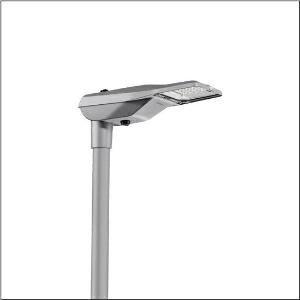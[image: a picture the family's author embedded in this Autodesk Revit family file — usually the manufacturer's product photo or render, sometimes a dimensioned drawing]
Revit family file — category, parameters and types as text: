
# Revit family: streetlight_sl_21_micro___st1_0a_5xe1d33t08db_ddb2
name_source: partatom
category: Lighting Fixtures
units: mm (PartAtom-declared; Revit-internal decimal feet)

## family parameters
Cut with Voids When Loaded = No
Host = Face
Light Source = No
Part Type = Normal
Room Calculation Point = No
Round Connector Dimension = Use Diameter
Shared = No

## types (1)
- --- (1 x LED, 5110 lm, 39.1 W, 3000K)
    Apparent Load = 39 VA
    CIE Flux Codes = 37 72 97 100 100
    Color Rendering = 70
    Color Temperature = 3000K
    Default Elevation = 1800 mm
    Description = Streetlight SL 21 micro, mast luminaire, primary light control with lens, of PMMA, primary optical cover: cover, of toughened safety glass, transparent, light distribution: ST1.0a, light emission: direct distribution, primary light characteristic: asymmetric, installation type: side-entry, post-top, LED, High Power LED, rated luminous flux: 5.110lm, luminous efficacy: 131lm/W, light colour: 730, colour temperature: 3000K, control: flexible luminous flux parameterisation, time-dependent luminous flux control, constant luminous flux control, overheat protection, presetting dimming logarithmic, mains connection: 220..240V, AC, 50/60Hz, start of lifetime: 39W, end of service life: 41W, reduction: 18W, luminaire housing, of diecast aluminium, powder-coated, Siteco® metallic grey (DB 702S), corrosivity category C5 mid according to DIN EN ISO 12944, please order mast flange separately, inclination adjustable: 0°, 5°, 10°, 15°, sealing non-destructively replaceable, multi-level sealing system, length: 528mm, width: 235mm, height: 110mm, mast flange for spigot size: 42mm (side-entry): 5XC10008XM4, 60/48mm (side-entry/post-top): 5XC10108XM2, 76/60mm (side-entry/post-top): 5XC10108XM1, Smart Interface below and above, protection rating (complete): IP66, insulation class (complete): insulation class II (safety insulation), certification: CE, ENEC, ENEC+, VDE, impact resistance: IK09, permissible operating ambient temperature for outdoor applications: -40..+50°C, standard-compliant lighting for roads and squares, packaging unit: 1 piece

Light Distribution: ST1.0a
    Height = 110 mm
    Lamp = 1 x LED
    Lamp Light Flux = 5110 lm
    Lamp Power = 39.1 W
    Lamp count = 1
    Length = 528 mm
    Luminous efficacy = 131 lm/W
    Manufacturer = Siteco
    ModVariant = No
    Model = 5XE1D33T08DB
    Number of Poles = 1
    OnlyDefault = Yes
    Power Factor = 1
    Product Name = Streetlight SL 21 micro | ST1.0a
    Product group = mast luminaire | pylon top
    ProductGroupID = 6100
    Protection Class = Protection class II
    Protection Degree = IP 66
    RLX_Detail_Level = 1
    RLX_Emergency_Light_Flux = 0 lm
    RLX_Emergency_Type = 0
    RLX_Emergency_Type_DB = No
    RlxData = <blob elided: 98605 chars, md5=bad2422d>
    Socket = socket
    Standby Power = 0 W
    System Light Flux = 5110 lm
    System Power = 39 W
    Type Comments = factory setting: luminous flux: 100 % | dim-lin: 254 | 765 mA
    Type Image = l_1007239.jpg
    URL = http://relux.com
    VarID = @adj_105915
    Voltage = 0 V
    Weight = 0.00 kg
    Width = 235 mm

## geometry (parser evidence)
native form markers: Blend x4, Sweep x11
no freeform markers — native parametric forms only
